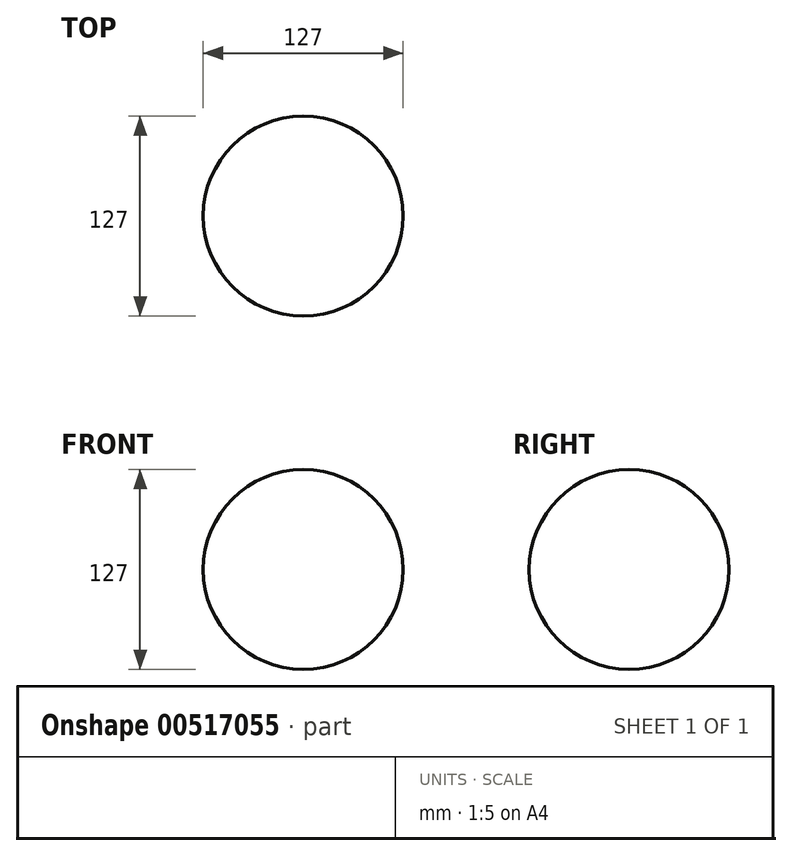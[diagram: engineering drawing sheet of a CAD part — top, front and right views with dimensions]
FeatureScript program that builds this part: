
annotation { "Feature Type Name" : "Feature", "Feature Type Description" : "" }
export const myFeature = defineFeature(function(context is Context, id is Id, definition is map)
    precondition{}
    {
        {
            var Q0;
            Q0=qCreatedBy(makeId("Top.planeOp"),FACE);
            var sketch = newSketch(context, id + "F0", { "sketchPlane" : qUnion([Q0])});
            skArc(sketch, "E0", {"start": v(-63.5, 0) * mm, "mid": v(0, -63.5) * mm, "end": v(63.5, 0) * mm});
            skLineSegment(sketch, "E1", {"start": v(63.5, 0) * mm, "end": v(-63.5, 0) * mm});
            skSolve(sketch);
        }
        {
            var Q0;
            Q0=makeQuery(id+"F0.imprint","IMPRINT",FACE,{"disambiguationData":[TD([[makeQuery(id+"F0.imprint","IMPRINT",EDGE,{"derivedFrom":sQuery(id+"F0.wireOp",EDGE,"E0")}),1.0]])]});
            var Q1;
            Q1=sQuery(id+"F0.wireOp",EDGE,"E1");
            revolve(context, id + "F1", {"entities" : qUnion([Q0]), "axis" : qUnion([Q1]), "revolveType" : RevolveType.FULL});
        }
    });
